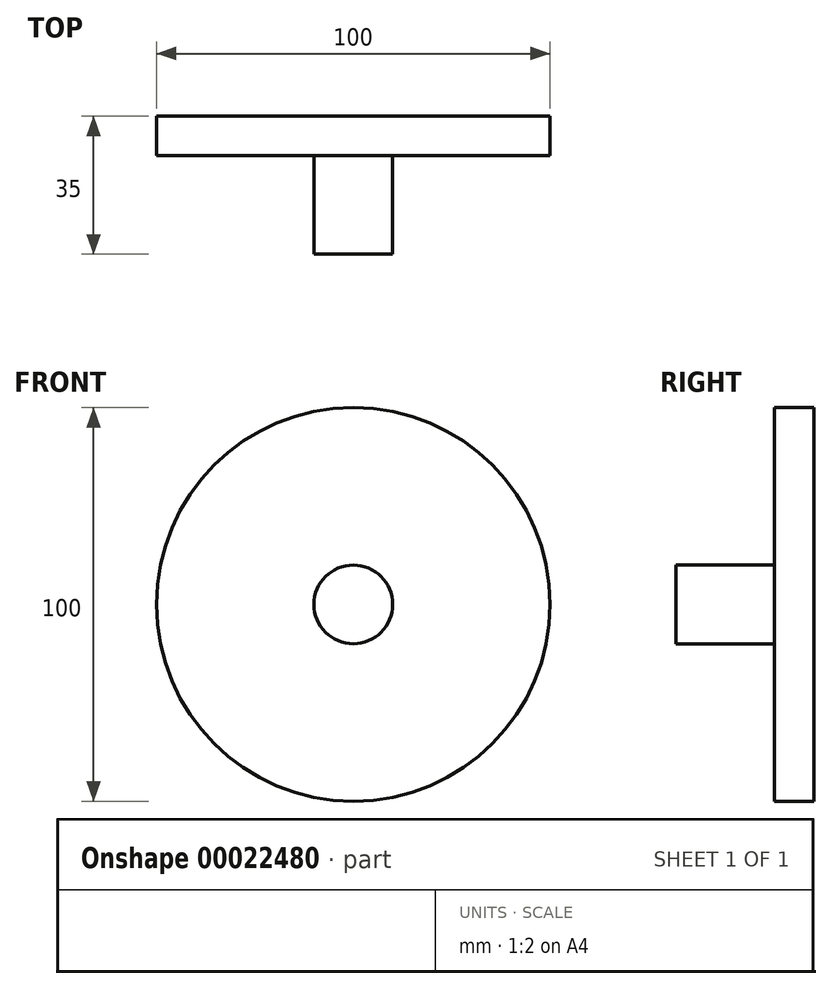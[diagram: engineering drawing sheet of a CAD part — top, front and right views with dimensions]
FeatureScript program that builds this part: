
annotation { "Feature Type Name" : "Feature", "Feature Type Description" : "" }
export const myFeature = defineFeature(function(context is Context, id is Id, definition is map)
    precondition{}
    {
        {
            var Q0;
            Q0=qCreatedBy(makeId("Front.planeOp"),FACE);
            var sketch = newSketch(context, id + "F0", { "sketchPlane" : qUnion([Q0])});
            skCircle(sketch, "E0", {"center": v(0, 0) * mm, "radius": 50 * mm});
            skSolve(sketch);
        }
        {
            var Q0;
            Q0=makeQuery(id+"F0.imprint","IMPRINT",FACE,{"disambiguationData":[TD([[makeQuery(id+"F0.imprint","IMPRINT",EDGE,{"derivedFrom":sQuery(id+"F0.wireOp",EDGE,"E0")}),1.0]])]});
            extrude(context, id + "F1", {"entities" : qUnion([Q0]), "depth" : 10 * mm});
        }
        {
            var Q0;
            Q0=makeQuery(id+"F1.opExtrude","CAP_FACE",FACE,{"disambiguationData":[OSD([sQuery(id+"F0.wireOp",EDGE,"E0")])],"isStart":false});
            var sketch = newSketch(context, id + "F2", { "sketchPlane" : qUnion([Q0])});
            skCircle(sketch, "E1", {"center": v(0, 0) * mm, "radius": 10 * mm});
            skSolve(sketch);
        }
        {
            var Q0;
            Q0=makeQuery(id+"F2.imprint","IMPRINT",FACE,{"disambiguationData":[TD([[makeQuery(id+"F2.imprint","IMPRINT",EDGE,{"derivedFrom":sQuery(id+"F2.wireOp",EDGE,"E1")}),1.0]])]});
            extrude(context, id + "F3", {"entities" : qUnion([Q0]), "operationType" : NewBodyOperationType.ADD, "depth" : 25 * mm});
        }
    });
